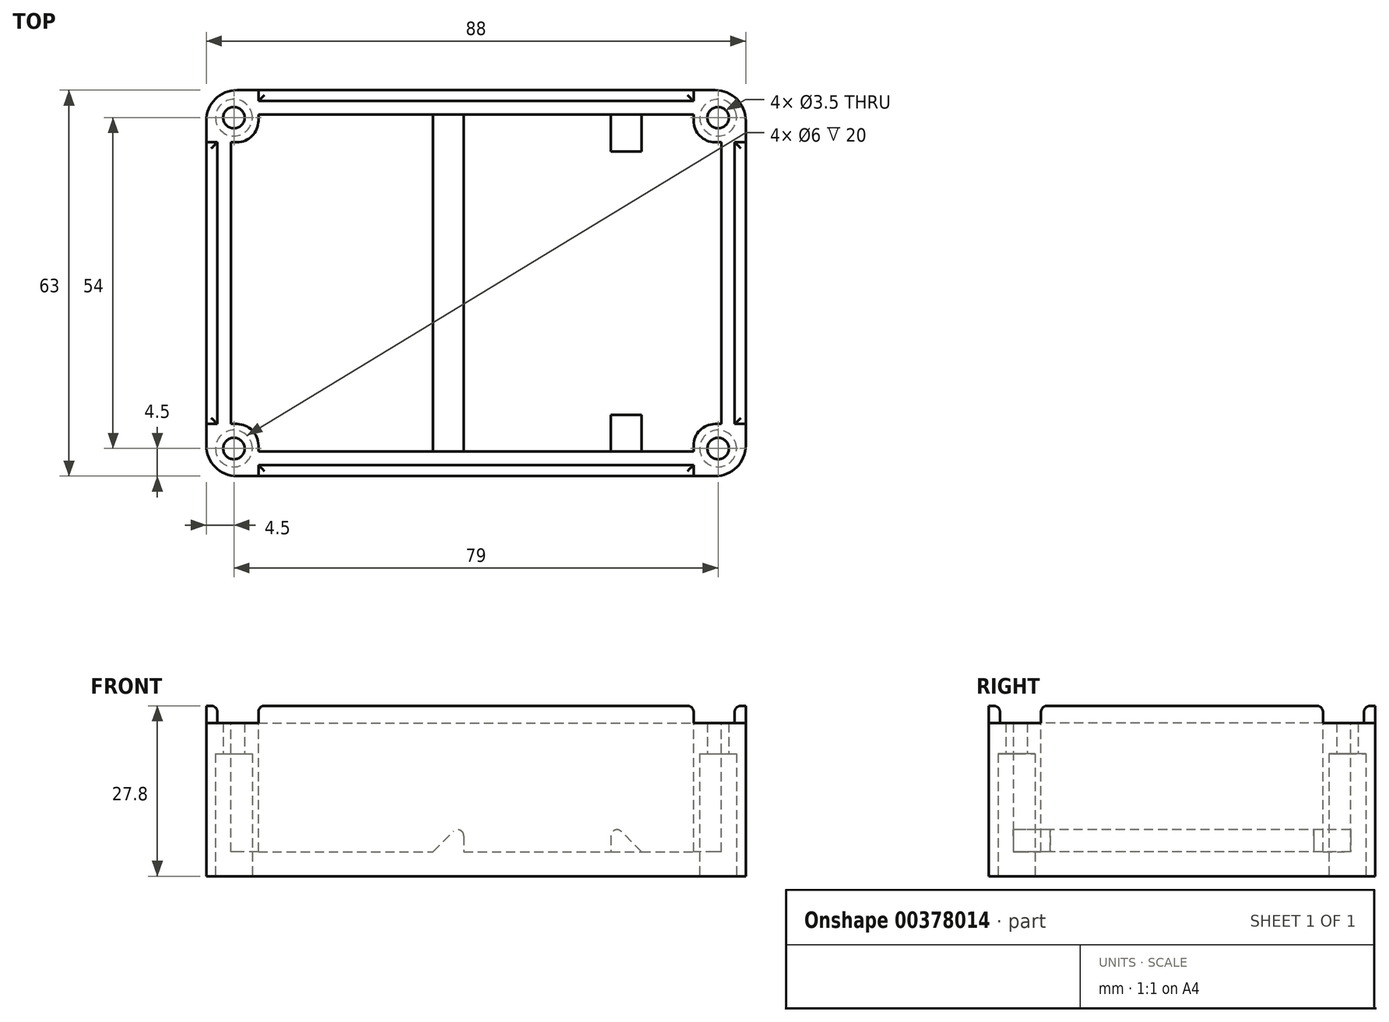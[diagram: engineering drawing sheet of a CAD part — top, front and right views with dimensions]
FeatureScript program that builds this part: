
annotation { "Feature Type Name" : "Feature", "Feature Type Description" : "" }
export const myFeature = defineFeature(function(context is Context, id is Id, definition is map)
    precondition{}
    {
        {
            var Q0;
            Q0=qCreatedBy(makeId("Top.planeOp"),FACE);
            cPlane(context, id + "F0", {"entities" : qUnion([Q0]), "cplaneType" : CPlaneType.OFFSET, "offset" : 21 * mm, "width" : 150 * mm, "height" : 150 * mm});
        }
        {
            var Q0;
            Q0=qCreatedBy(makeId("Top.planeOp"),FACE);
            var sketch = newSketch(context, id + "F1", { "sketchPlane" : qUnion([Q0])});
            skLineSegment(sketch, "E0.bottom", {"start": v(-80, 0) * mm, "end": v(0, 0) * mm});
            skLineSegment(sketch, "E0.top", {"start": v(-80, -55) * mm, "end": v(0, -55) * mm});
            skLineSegment(sketch, "E0.left", {"start": v(-80, 0) * mm, "end": v(-80, -55) * mm});
            skLineSegment(sketch, "E0.right", {"start": v(0, 0) * mm, "end": v(0, -55) * mm});
            skSolve(sketch);
        }
        {
            var Q0;
            Q0=makeQuery(id+"F1.imprint","IMPRINT",FACE,{"disambiguationData":[TD([[makeQuery(id+"F1.imprint","IMPRINT",EDGE,{"derivedFrom":sQuery(id+"F1.wireOp",EDGE,"E0.bottom")}),-1.0]])]});
            extrude(context, id + "F2", {"entities" : qUnion([Q0]), "depth" : 21 * mm});
        }
        {
            var Q0;
            Q0=makeQuery(id+"F2.opExtrude","CAP_FACE",FACE,{"disambiguationData":[OSD([sQuery(id+"F1.wireOp",EDGE,"E0.bottom"),sQuery(id+"F1.wireOp",EDGE,"E0.top"),sQuery(id+"F1.wireOp",EDGE,"E0.left"),sQuery(id+"F1.wireOp",EDGE,"E0.right")])],"isStart":false});
            shell(context, id + "F3", {"entities" : qUnion([Q0]), "thickness" : 4 * mm, "oppositeDirection" : true});
        }
        {
            var Q0;
            Q0=makeQuery(id+"F3.opShell","OFFSET_FACE",FACE,{"disambiguationData":[OSD([sQuery(id+"F1.wireOp",EDGE,"E0.bottom"),sQuery(id+"F1.wireOp",EDGE,"E0.top"),sQuery(id+"F1.wireOp",EDGE,"E0.left"),sQuery(id+"F1.wireOp",EDGE,"E0.right")])]});
            var sketch = newSketch(context, id + "F4", { "sketchPlane" : qUnion([Q0])});
            skLineSegment(sketch, "E1.bottom", {"start": v(-47, 0) * mm, "end": v(-42, 0) * mm});
            skLineSegment(sketch, "E1.top", {"start": v(-47, -55) * mm, "end": v(-42, -55) * mm});
            skLineSegment(sketch, "E1.left", {"start": v(-47, 0) * mm, "end": v(-47, -55) * mm});
            skLineSegment(sketch, "E1.right", {"start": v(-42, 0) * mm, "end": v(-42, -55) * mm});
            skSolve(sketch);
        }
        {
            var Q0;
            Q0=qSketchRegion(id+"F4",true);
            extrude(context, id + "F5", {"entities" : qUnion([Q0]), "operationType" : NewBodyOperationType.ADD, "depth" : 5 * mm});
        }
        {
            var Q0;
            {var subQ0=sQuery(id+"F1.wireOp",EDGE,"E0.bottom");var subQ1=sQuery(id+"F1.wireOp",EDGE,"E0.top");var subQ2=sQuery(id+"F1.wireOp",EDGE,"E0.right");Q0=makeQuery(id+"F5.boolean.opBoolean","SPLIT",FACE,{"disambiguationData":[TD([makeQuery(id+"F3.opShell","OFFSET_FACE",FACE,{"disambiguationData":[OSD([subQ2])]})])],"derivedFrom":makeQuery(id+"F3.opShell","OFFSET_FACE",FACE,{"disambiguationData":[OSD([subQ0,subQ1,sQuery(id+"F1.wireOp",EDGE,"E0.left"),subQ2])]})});}
            var sketch = newSketch(context, id + "F6", { "sketchPlane" : qUnion([Q0])});
            skLineSegment(sketch, "E2.bottom", {"start": v(-18, 0) * mm, "end": v(-13, 0) * mm});
            skLineSegment(sketch, "E2.top", {"start": v(-18, -6) * mm, "end": v(-13, -6) * mm});
            skLineSegment(sketch, "E2.left", {"start": v(-18, 0) * mm, "end": v(-18, -6) * mm});
            skLineSegment(sketch, "E2.right", {"start": v(-13, 0) * mm, "end": v(-13, -6) * mm});
            skLineSegment(sketch, "E3.bottom", {"start": v(-18, -49) * mm, "end": v(-13, -49) * mm});
            skLineSegment(sketch, "E3.top", {"start": v(-18, -55) * mm, "end": v(-13, -55) * mm});
            skLineSegment(sketch, "E3.left", {"start": v(-18, -49) * mm, "end": v(-18, -55) * mm});
            skLineSegment(sketch, "E3.right", {"start": v(-13, -49) * mm, "end": v(-13, -55) * mm});
            skSolve(sketch);
        }
        {
            var Q0;
            Q0=qSketchRegion(id+"F6",true);
            extrude(context, id + "F7", {"entities" : qUnion([Q0]), "operationType" : NewBodyOperationType.ADD, "depth" : 5 * mm});
        }
        {
            var Q0;
            Q0=qCreatedBy(id+"F0.planeOp",FACE);
            var sketch = newSketch(context, id + "F8", { "sketchPlane" : qUnion([Q0])});
            skLineSegment(sketch, "E4.bottom", {"start": v(-84, 4) * mm, "end": v(4, 4) * mm});
            skLineSegment(sketch, "E4.top", {"start": v(-84, -59) * mm, "end": v(4, -59) * mm});
            skLineSegment(sketch, "E4.left", {"start": v(-84, 4) * mm, "end": v(-84, -59) * mm});
            skLineSegment(sketch, "E4.right", {"start": v(4, 4) * mm, "end": v(4, -59) * mm});
            skLineSegment(sketch, "E5.bottom", {"start": v(-82.2, 2.2) * mm, "end": v(2.2, 2.2) * mm});
            skLineSegment(sketch, "E5.top", {"start": v(-82.2, -57.2) * mm, "end": v(2.2, -57.2) * mm});
            skLineSegment(sketch, "E5.left", {"start": v(-82.2, 2.2) * mm, "end": v(-82.2, -57.2) * mm});
            skLineSegment(sketch, "E5.right", {"start": v(2.2, 2.2) * mm, "end": v(2.2, -57.2) * mm});
            skSolve(sketch);
        }
        {
            var Q0;
            Q0=qSketchRegion(id+"F8",true);
            extrude(context, id + "F9", {"entities" : qUnion([Q0]), "operationType" : NewBodyOperationType.ADD, "depth" : 2.8 * mm});
        }
        {
            var Q0;
            Q0=qCreatedBy(id+"F0.planeOp",FACE);
            var sketch = newSketch(context, id + "F10", { "sketchPlane" : qUnion([Q0])});
            skLineSegment(sketch, "E6", {"start": v(-79, -4.5) * mm, "end": v(-84, -4.5) * mm});
            skLineSegment(sketch, "E7", {"start": v(-84, -4.5) * mm, "end": v(-84, 4) * mm});
            skLineSegment(sketch, "E8", {"start": v(-84, 4) * mm, "end": v(-75.5, 4) * mm});
            skLineSegment(sketch, "E9", {"start": v(-75.5, 4) * mm, "end": v(-75.5, -1) * mm});
            skArc(sketch, "E10", {"start": v(-79, -4.5) * mm, "mid": v(-76.53, -3.47) * mm, "end": v(-75.5, -1) * mm});
            skLineSegment(sketch, "E11", {"start": v(-1, -4.5) * mm, "end": v(4, -4.5) * mm});
            skLineSegment(sketch, "E12", {"start": v(4, -4.5) * mm, "end": v(4, 4) * mm});
            skLineSegment(sketch, "E13", {"start": v(4, 4) * mm, "end": v(-4.5, 4) * mm});
            skLineSegment(sketch, "E14", {"start": v(-4.5, 4) * mm, "end": v(-4.5, -1) * mm});
            skArc(sketch, "E15", {"start": v(-4.5, -1) * mm, "mid": v(-3.47, -3.47) * mm, "end": v(-1, -4.5) * mm});
            skLineSegment(sketch, "E16", {"start": v(-4.5, -54) * mm, "end": v(-4.5, -59) * mm});
            skLineSegment(sketch, "E17", {"start": v(-4.5, -59) * mm, "end": v(4, -59) * mm});
            skLineSegment(sketch, "E18", {"start": v(4, -59) * mm, "end": v(4, -50.5) * mm});
            skLineSegment(sketch, "E19", {"start": v(4, -50.5) * mm, "end": v(-1, -50.5) * mm});
            skArc(sketch, "E20", {"start": v(-1, -50.5) * mm, "mid": v(-3.47, -51.53) * mm, "end": v(-4.5, -54) * mm});
            skLineSegment(sketch, "E21", {"start": v(-79, -50.5) * mm, "end": v(-84, -50.5) * mm});
            skLineSegment(sketch, "E22", {"start": v(-84, -50.5) * mm, "end": v(-84, -59) * mm});
            skLineSegment(sketch, "E23", {"start": v(-84, -59) * mm, "end": v(-75.5, -59) * mm});
            skLineSegment(sketch, "E24", {"start": v(-75.5, -59) * mm, "end": v(-75.5, -54) * mm});
            skArc(sketch, "E25", {"start": v(-75.5, -54) * mm, "mid": v(-76.53, -51.53) * mm, "end": v(-79, -50.5) * mm});
            skSolve(sketch);
        }
        {
            var Q0;
            Q0=qSketchRegion(id+"F10",true);
            extrude(context, id + "F11", {"entities" : qUnion([Q0]), "operationType" : NewBodyOperationType.ADD, "oppositeDirection" : true, "depth" : 22 * mm});
        }
        {
            var Q0;
            Q0=qSketchRegion(id+"F10",true);
            extrude(context, id + "F12", {"entities" : qUnion([Q0]), "operationType" : NewBodyOperationType.REMOVE, "depth" : 3 * mm});
        }
        {
            var Q0;
            Q0=makeQuery(id+"F2.opExtrude","CAP_FACE",FACE,{"disambiguationData":[OSD([sQuery(id+"F1.wireOp",EDGE,"E0.bottom"),sQuery(id+"F1.wireOp",EDGE,"E0.top"),sQuery(id+"F1.wireOp",EDGE,"E0.left"),sQuery(id+"F1.wireOp",EDGE,"E0.right")])],"isStart":true});
            var sketch = newSketch(context, id + "F13", { "sketchPlane" : qUnion([Q0])});
            skPoint(sketch, "E26", {"position": v(-79.5, 0.5) * mm});
            skPoint(sketch, "E27", {"position": v(-0.5, 0.5) * mm});
            skPoint(sketch, "E28", {"position": v(-0.5, 54.5) * mm});
            skPoint(sketch, "E29", {"position": v(-79.5, 54.5) * mm});
            skSolve(sketch);
        }
        {
            var Q0;
            Q0=sQuery(id+"F13.wireOp",VERTEX,"E26");
            var Q1;
            Q1=sQuery(id+"F13.wireOp",VERTEX,"E27");
            var Q2;
            Q2=sQuery(id+"F13.wireOp",VERTEX,"E28");
            var Q3;
            Q3=sQuery(id+"F13.wireOp",VERTEX,"E29");
            var Q4;
            Q4=makeQuery(id+"F2.opExtrude","SWEPT_BODY",BODY,{"disambiguationData":[OSD([sQuery(id+"F1.wireOp",EDGE,"E0.bottom"),sQuery(id+"F1.wireOp",EDGE,"E0.top"),sQuery(id+"F1.wireOp",EDGE,"E0.left"),sQuery(id+"F1.wireOp",EDGE,"E0.right")])]});
            hole(context, id + "F14", {"style" : HoleStyle.C_BORE, "endStyle" : HoleEndStyle.THROUGH, "holeDiameter" : 3.5 * mm, "cBoreDiameter" : 6 * mm, "cBoreDepth" : 20 * mm, "tappedDepth" : 12 * mm, "tapClearance" : 3, "locations" : qUnion([Q0, Q1, Q2, Q3]), "scope" : qUnion([Q4])});
        }
        {
            var Q0;
            Q0=makeQuery(id+"F5.opExtrude","CAP_EDGE",EDGE,{"disambiguationData":[OSD([sQuery(id+"F4.wireOp",EDGE,"E1.left")])],"isStart":false});
            var Q1;
            Q1=makeQuery(id+"F7.opExtrude","CAP_EDGE",EDGE,{"disambiguationData":[OSD([sQuery(id+"F6.wireOp",EDGE,"E2.right")])],"isStart":false});
            var Q2;
            Q2=makeQuery(id+"F7.opExtrude","CAP_EDGE",EDGE,{"disambiguationData":[OSD([sQuery(id+"F6.wireOp",EDGE,"E3.right")])],"isStart":false});
            chamfer(context, id + "F15", {"entities" : qUnion([Q0, Q1, Q2]), "width" : 5 * mm, "tangentPropagation" : true});
        }
        {
            var Q0;
            Q0=makeQuery(id+"F9.boolean.opBoolean","MERGE",EDGE,{"derivedFrom":[makeQuery(id+"F2.opExtrude","SWEPT_EDGE",EDGE,{"disambiguationData":[OSD([sQuery(id+"F1.wireOp",EDGE,"E0.bottom"),sQuery(id+"F1.wireOp",EDGE,"E0.right")])]}),makeQuery(id+"F9.opExtrude","SWEPT_EDGE",EDGE,{"disambiguationData":[OSD([sQuery(id+"F8.wireOp",EDGE,"E4.bottom"),sQuery(id+"F8.wireOp",EDGE,"E4.right")])]})]});
            var Q1;
            Q1=makeQuery(id+"F9.boolean.opBoolean","MERGE",EDGE,{"derivedFrom":[makeQuery(id+"F2.opExtrude","SWEPT_EDGE",EDGE,{"disambiguationData":[OSD([sQuery(id+"F1.wireOp",EDGE,"E0.bottom"),sQuery(id+"F1.wireOp",EDGE,"E0.left")])]}),makeQuery(id+"F9.opExtrude","SWEPT_EDGE",EDGE,{"disambiguationData":[OSD([sQuery(id+"F8.wireOp",EDGE,"E4.bottom"),sQuery(id+"F8.wireOp",EDGE,"E4.left")])]})]});
            var Q2;
            Q2=makeQuery(id+"F9.boolean.opBoolean","MERGE",EDGE,{"derivedFrom":[makeQuery(id+"F2.opExtrude","SWEPT_EDGE",EDGE,{"disambiguationData":[OSD([sQuery(id+"F1.wireOp",EDGE,"E0.top"),sQuery(id+"F1.wireOp",EDGE,"E0.left")])]}),makeQuery(id+"F9.opExtrude","SWEPT_EDGE",EDGE,{"disambiguationData":[OSD([sQuery(id+"F8.wireOp",EDGE,"E4.top"),sQuery(id+"F8.wireOp",EDGE,"E4.left")])]})]});
            var Q3;
            Q3=makeQuery(id+"F9.boolean.opBoolean","MERGE",EDGE,{"derivedFrom":[makeQuery(id+"F2.opExtrude","SWEPT_EDGE",EDGE,{"disambiguationData":[OSD([sQuery(id+"F1.wireOp",EDGE,"E0.top"),sQuery(id+"F1.wireOp",EDGE,"E0.right")])]}),makeQuery(id+"F9.opExtrude","SWEPT_EDGE",EDGE,{"disambiguationData":[OSD([sQuery(id+"F8.wireOp",EDGE,"E4.top"),sQuery(id+"F8.wireOp",EDGE,"E4.right")])]})]});
            fillet(context, id + "F16", {"entities" : qUnion([Q0, Q1, Q2, Q3]), "radius" : 5 * mm, "tangentPropagation" : true, "allowEdgeOverflow" : false});
        }
        {
            var Q0;
            Q0=makeQuery(id+"F9.opExtrude","CAP_EDGE",EDGE,{"disambiguationData":[OSD([sQuery(id+"F8.wireOp",EDGE,"E5.bottom")])],"isStart":false});
            var Q1;
            Q1=makeQuery(id+"F9.opExtrude","CAP_EDGE",EDGE,{"disambiguationData":[OSD([sQuery(id+"F8.wireOp",EDGE,"E5.left")])],"isStart":false});
            var Q2;
            Q2=makeQuery(id+"F9.opExtrude","CAP_EDGE",EDGE,{"disambiguationData":[OSD([sQuery(id+"F8.wireOp",EDGE,"E5.top")])],"isStart":false});
            var Q3;
            Q3=makeQuery(id+"F9.opExtrude","CAP_EDGE",EDGE,{"disambiguationData":[OSD([sQuery(id+"F8.wireOp",EDGE,"E5.right")])],"isStart":false});
            var Q4;
            Q4=makeQuery(id+"F12.boolean.opBoolean","COPY",EDGE,{"derivedFrom":makeQuery(id+"F12.opExtrude","CAP_EDGE",EDGE,{"disambiguationData":[OSD([sQuery(id+"F10.wireOp",EDGE,"E6")])],"isStart":false})});
            var Q5;
            Q5=makeQuery(id+"F12.boolean.opBoolean","COPY",EDGE,{"derivedFrom":makeQuery(id+"F12.opExtrude","CAP_EDGE",EDGE,{"disambiguationData":[OSD([sQuery(id+"F10.wireOp",EDGE,"E9")])],"isStart":false})});
            var Q6;
            Q6=makeQuery(id+"F12.boolean.opBoolean","COPY",EDGE,{"derivedFrom":makeQuery(id+"F12.opExtrude","CAP_EDGE",EDGE,{"disambiguationData":[OSD([sQuery(id+"F10.wireOp",EDGE,"E14")])],"isStart":false})});
            var Q7;
            Q7=makeQuery(id+"F12.boolean.opBoolean","COPY",EDGE,{"derivedFrom":makeQuery(id+"F12.opExtrude","CAP_EDGE",EDGE,{"disambiguationData":[OSD([sQuery(id+"F10.wireOp",EDGE,"E11")])],"isStart":false})});
            var Q8;
            Q8=makeQuery(id+"F12.boolean.opBoolean","COPY",EDGE,{"derivedFrom":makeQuery(id+"F12.opExtrude","CAP_EDGE",EDGE,{"disambiguationData":[OSD([sQuery(id+"F10.wireOp",EDGE,"E19")])],"isStart":false})});
            var Q9;
            Q9=makeQuery(id+"F12.boolean.opBoolean","COPY",EDGE,{"derivedFrom":makeQuery(id+"F12.opExtrude","CAP_EDGE",EDGE,{"disambiguationData":[OSD([sQuery(id+"F10.wireOp",EDGE,"E24")])],"isStart":false})});
            var Q10;
            Q10=makeQuery(id+"F12.boolean.opBoolean","COPY",EDGE,{"derivedFrom":makeQuery(id+"F12.opExtrude","CAP_EDGE",EDGE,{"disambiguationData":[OSD([sQuery(id+"F10.wireOp",EDGE,"E16")])],"isStart":false})});
            var Q11;
            Q11=makeQuery(id+"F12.boolean.opBoolean","COPY",EDGE,{"derivedFrom":makeQuery(id+"F12.opExtrude","CAP_EDGE",EDGE,{"disambiguationData":[OSD([sQuery(id+"F10.wireOp",EDGE,"E21")])],"isStart":false})});
            var Q12;
            Q12=makeQuery(id+"F12.boolean.opBoolean","INTERSECT",EDGE,{"derivedFrom":[makeQuery(id+"F9.opExtrude","CAP_FACE",FACE,{"disambiguationData":[OSD([sQuery(id+"F8.wireOp",EDGE,"E4.bottom"),sQuery(id+"F8.wireOp",EDGE,"E4.top"),sQuery(id+"F8.wireOp",EDGE,"E4.left"),sQuery(id+"F8.wireOp",EDGE,"E4.right"),sQuery(id+"F8.wireOp",EDGE,"E5.bottom"),sQuery(id+"F8.wireOp",EDGE,"E5.top"),sQuery(id+"F8.wireOp",EDGE,"E5.left"),sQuery(id+"F8.wireOp",EDGE,"E5.right")])],"isStart":false}),makeQuery(id+"F12.opExtrude","SWEPT_FACE",FACE,{"disambiguationData":[OSD([sQuery(id+"F10.wireOp",EDGE,"E9")])]})]});
            var Q13;
            Q13=makeQuery(id+"F12.boolean.opBoolean","INTERSECT",EDGE,{"derivedFrom":[makeQuery(id+"F9.opExtrude","CAP_FACE",FACE,{"disambiguationData":[OSD([sQuery(id+"F8.wireOp",EDGE,"E4.bottom"),sQuery(id+"F8.wireOp",EDGE,"E4.top"),sQuery(id+"F8.wireOp",EDGE,"E4.left"),sQuery(id+"F8.wireOp",EDGE,"E4.right"),sQuery(id+"F8.wireOp",EDGE,"E5.bottom"),sQuery(id+"F8.wireOp",EDGE,"E5.top"),sQuery(id+"F8.wireOp",EDGE,"E5.left"),sQuery(id+"F8.wireOp",EDGE,"E5.right")])],"isStart":false}),makeQuery(id+"F12.opExtrude","SWEPT_FACE",FACE,{"disambiguationData":[OSD([sQuery(id+"F10.wireOp",EDGE,"E14")])]})]});
            var Q14;
            Q14=makeQuery(id+"F12.boolean.opBoolean","INTERSECT",EDGE,{"derivedFrom":[makeQuery(id+"F9.opExtrude","CAP_FACE",FACE,{"disambiguationData":[OSD([sQuery(id+"F8.wireOp",EDGE,"E4.bottom"),sQuery(id+"F8.wireOp",EDGE,"E4.top"),sQuery(id+"F8.wireOp",EDGE,"E4.left"),sQuery(id+"F8.wireOp",EDGE,"E4.right"),sQuery(id+"F8.wireOp",EDGE,"E5.bottom"),sQuery(id+"F8.wireOp",EDGE,"E5.top"),sQuery(id+"F8.wireOp",EDGE,"E5.left"),sQuery(id+"F8.wireOp",EDGE,"E5.right")])],"isStart":false}),makeQuery(id+"F12.opExtrude","SWEPT_FACE",FACE,{"disambiguationData":[OSD([sQuery(id+"F10.wireOp",EDGE,"E11")])]})]});
            var Q15;
            Q15=makeQuery(id+"F12.boolean.opBoolean","INTERSECT",EDGE,{"derivedFrom":[makeQuery(id+"F9.opExtrude","CAP_FACE",FACE,{"disambiguationData":[OSD([sQuery(id+"F8.wireOp",EDGE,"E4.bottom"),sQuery(id+"F8.wireOp",EDGE,"E4.top"),sQuery(id+"F8.wireOp",EDGE,"E4.left"),sQuery(id+"F8.wireOp",EDGE,"E4.right"),sQuery(id+"F8.wireOp",EDGE,"E5.bottom"),sQuery(id+"F8.wireOp",EDGE,"E5.top"),sQuery(id+"F8.wireOp",EDGE,"E5.left"),sQuery(id+"F8.wireOp",EDGE,"E5.right")])],"isStart":false}),makeQuery(id+"F12.opExtrude","SWEPT_FACE",FACE,{"disambiguationData":[OSD([sQuery(id+"F10.wireOp",EDGE,"E19")])]})]});
            var Q16;
            Q16=makeQuery(id+"F12.boolean.opBoolean","INTERSECT",EDGE,{"derivedFrom":[makeQuery(id+"F9.opExtrude","CAP_FACE",FACE,{"disambiguationData":[OSD([sQuery(id+"F8.wireOp",EDGE,"E4.bottom"),sQuery(id+"F8.wireOp",EDGE,"E4.top"),sQuery(id+"F8.wireOp",EDGE,"E4.left"),sQuery(id+"F8.wireOp",EDGE,"E4.right"),sQuery(id+"F8.wireOp",EDGE,"E5.bottom"),sQuery(id+"F8.wireOp",EDGE,"E5.top"),sQuery(id+"F8.wireOp",EDGE,"E5.left"),sQuery(id+"F8.wireOp",EDGE,"E5.right")])],"isStart":false}),makeQuery(id+"F12.opExtrude","SWEPT_FACE",FACE,{"disambiguationData":[OSD([sQuery(id+"F10.wireOp",EDGE,"E16")])]})]});
            var Q17;
            Q17=makeQuery(id+"F12.boolean.opBoolean","INTERSECT",EDGE,{"derivedFrom":[makeQuery(id+"F9.opExtrude","CAP_FACE",FACE,{"disambiguationData":[OSD([sQuery(id+"F8.wireOp",EDGE,"E4.bottom"),sQuery(id+"F8.wireOp",EDGE,"E4.top"),sQuery(id+"F8.wireOp",EDGE,"E4.left"),sQuery(id+"F8.wireOp",EDGE,"E4.right"),sQuery(id+"F8.wireOp",EDGE,"E5.bottom"),sQuery(id+"F8.wireOp",EDGE,"E5.top"),sQuery(id+"F8.wireOp",EDGE,"E5.left"),sQuery(id+"F8.wireOp",EDGE,"E5.right")])],"isStart":false}),makeQuery(id+"F12.opExtrude","SWEPT_FACE",FACE,{"disambiguationData":[OSD([sQuery(id+"F10.wireOp",EDGE,"E21")])]})]});
            var Q18;
            Q18=makeQuery(id+"F12.boolean.opBoolean","INTERSECT",EDGE,{"derivedFrom":[makeQuery(id+"F9.opExtrude","CAP_FACE",FACE,{"disambiguationData":[OSD([sQuery(id+"F8.wireOp",EDGE,"E4.bottom"),sQuery(id+"F8.wireOp",EDGE,"E4.top"),sQuery(id+"F8.wireOp",EDGE,"E4.left"),sQuery(id+"F8.wireOp",EDGE,"E4.right"),sQuery(id+"F8.wireOp",EDGE,"E5.bottom"),sQuery(id+"F8.wireOp",EDGE,"E5.top"),sQuery(id+"F8.wireOp",EDGE,"E5.left"),sQuery(id+"F8.wireOp",EDGE,"E5.right")])],"isStart":false}),makeQuery(id+"F12.opExtrude","SWEPT_FACE",FACE,{"disambiguationData":[OSD([sQuery(id+"F10.wireOp",EDGE,"E24")])]})]});
            var Q19;
            Q19=makeQuery(id+"F12.boolean.opBoolean","INTERSECT",EDGE,{"derivedFrom":[makeQuery(id+"F9.opExtrude","CAP_FACE",FACE,{"disambiguationData":[OSD([sQuery(id+"F8.wireOp",EDGE,"E4.bottom"),sQuery(id+"F8.wireOp",EDGE,"E4.top"),sQuery(id+"F8.wireOp",EDGE,"E4.left"),sQuery(id+"F8.wireOp",EDGE,"E4.right"),sQuery(id+"F8.wireOp",EDGE,"E5.bottom"),sQuery(id+"F8.wireOp",EDGE,"E5.top"),sQuery(id+"F8.wireOp",EDGE,"E5.left"),sQuery(id+"F8.wireOp",EDGE,"E5.right")])],"isStart":false}),makeQuery(id+"F12.opExtrude","SWEPT_FACE",FACE,{"disambiguationData":[OSD([sQuery(id+"F10.wireOp",EDGE,"E6")])]})]});
            fillet(context, id + "F17", {"entities" : qUnion([Q0, Q1, Q2, Q3, Q4, Q5, Q6, Q7, Q8, Q9, Q10, Q11, Q12, Q13, Q14, Q15, Q16, Q17, Q18, Q19]), "radius" : 1 * mm, "tangentPropagation" : true, "allowEdgeOverflow" : false});
        }
        {
            var Q0;
            Q0=makeQuery(id+"F15.opChamfer","BLEND_EDGE",EDGE,{"blendedFrom":[makeQuery(id+"F5.opExtrude","CAP_EDGE",EDGE,{"disambiguationData":[OSD([sQuery(id+"F4.wireOp",EDGE,"E1.left")])],"isStart":false}),makeQuery(id+"F5.opExtrude","SWEPT_FACE",FACE,{"disambiguationData":[OSD([sQuery(id+"F4.wireOp",EDGE,"E1.right")])]})],"blendedInto":[makeQuery(id+"F5.opExtrude","SWEPT_FACE",FACE,{"disambiguationData":[OSD([sQuery(id+"F4.wireOp",EDGE,"E1.right")])]})]});
            var Q1;
            Q1=makeQuery(id+"F15.opChamfer","BLEND_EDGE",EDGE,{"blendedFrom":[makeQuery(id+"F7.opExtrude","CAP_EDGE",EDGE,{"disambiguationData":[OSD([sQuery(id+"F6.wireOp",EDGE,"E2.right")])],"isStart":false}),makeQuery(id+"F7.opExtrude","SWEPT_FACE",FACE,{"disambiguationData":[OSD([sQuery(id+"F6.wireOp",EDGE,"E2.left")])]})],"blendedInto":[makeQuery(id+"F7.opExtrude","SWEPT_FACE",FACE,{"disambiguationData":[OSD([sQuery(id+"F6.wireOp",EDGE,"E2.left")])]})]});
            var Q2;
            Q2=makeQuery(id+"F15.opChamfer","BLEND_EDGE",EDGE,{"blendedFrom":[makeQuery(id+"F7.opExtrude","CAP_EDGE",EDGE,{"disambiguationData":[OSD([sQuery(id+"F6.wireOp",EDGE,"E3.right")])],"isStart":false}),makeQuery(id+"F7.opExtrude","SWEPT_FACE",FACE,{"disambiguationData":[OSD([sQuery(id+"F6.wireOp",EDGE,"E3.left")])]})],"blendedInto":[makeQuery(id+"F7.opExtrude","SWEPT_FACE",FACE,{"disambiguationData":[OSD([sQuery(id+"F6.wireOp",EDGE,"E3.left")])]})]});
            fillet(context, id + "F18", {"entities" : qUnion([Q0, Q1, Q2]), "radius" : 1 * mm, "tangentPropagation" : true, "allowEdgeOverflow" : false});
        }
    });
